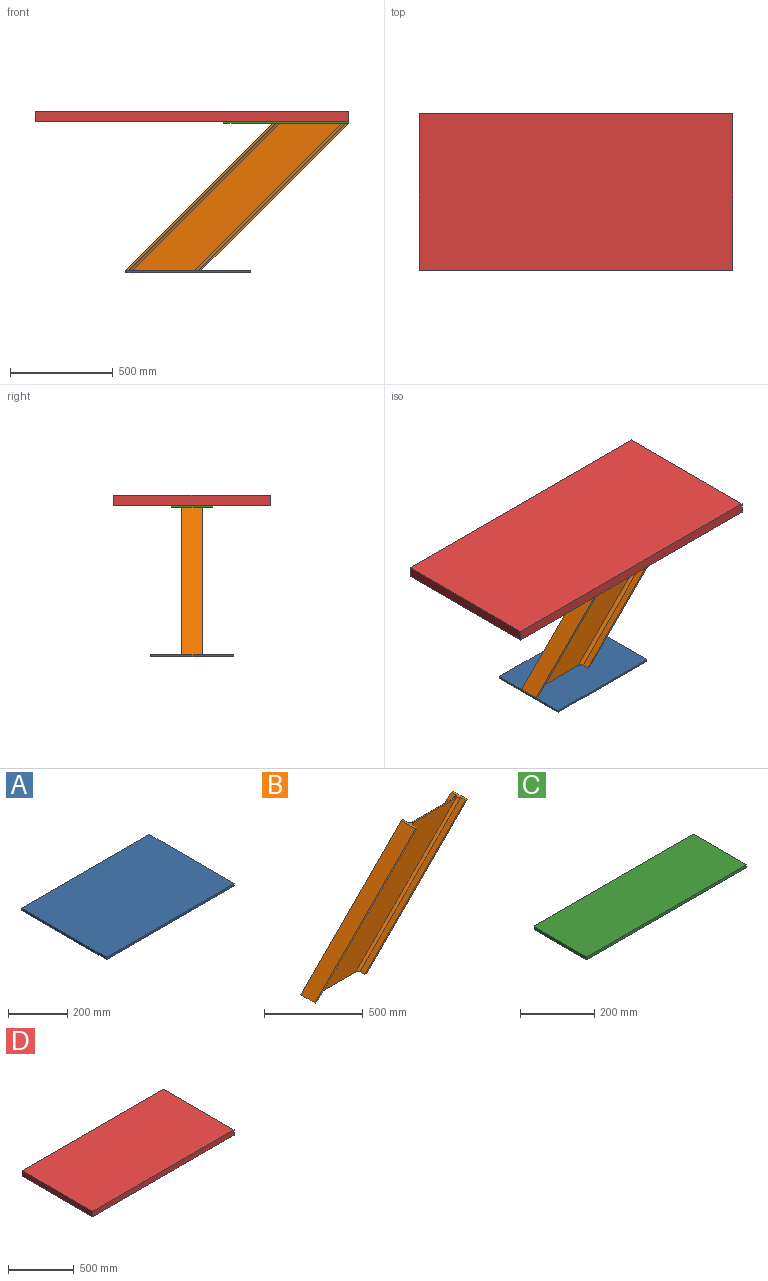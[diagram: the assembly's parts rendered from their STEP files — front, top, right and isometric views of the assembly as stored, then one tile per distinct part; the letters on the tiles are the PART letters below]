
ASSEMBLY  parts=4 mates=3
PART A: 10 faces, bbox 609.6x406.4x9.5 mm
  f0: plane 400.05x9.53mm, normal (1,0,0), area 3810.5mm2, adj f1,f7,f8,f9
  f1: cylinder r=3.17mm len=9.53mm, axis (0,0,-1), area 47.5mm2, adj f0,f2,f8,f9
  f2: plane 603.25x9.53mm, normal (0,1,0), area 5746mm2, adj f1,f3,f8,f9
  f3: cylinder r=3.17mm len=9.53mm, axis (0,0,-1), area 47.5mm2, adj f2,f4,f8,f9
  f4: plane 400.05x9.53mm, normal (-1,0,0), area 3810.5mm2, adj f3,f5,f8,f9
  f5: cylinder r=3.17mm len=9.53mm, axis (0,0,-1), area 47.5mm2, adj f4,f6,f8,f9
  f6: plane 603.25x9.53mm, normal (0,-1,0), area 5746mm2, adj f5,f7,f8,f9
  f7: cylinder r=3.17mm len=9.53mm, axis (0,0,-1), area 47.5mm2, adj f0,f6,f8,f9
  f8: plane 609.6x406.4mm, normal (0,0,1), area 247732.8mm2, adj f0,f1,f2,f3,f4,f5,f6,f7
  f9: plane 609.6x406.4mm, normal (0,0,-1), area 247732.8mm2, adj f0,f1,f2,f3,f4,f5,f6,f7
PART B: 19 faces, bbox 1086.6x101.6x738.6 mm
  f0: cylinder r=14.29mm len=738.63mm, axis (0.71,0,0.71), area 22801.8mm2, adj f1,f16,f17,f18
  f1: plane 1019.26x718.42mm, normal (0,1,0), area 216128.6mm2, adj f0,f2,f17,f18
  f2: cylinder r=14.29mm len=738.63mm, axis (0.71,0,0.71), area 22801.8mm2, adj f1,f3,f17,f18
  f3: plane 718.42x718.42mm, normal (0.71,0,-0.71), area 32245.1mm2, adj f2,f4,f17,f18
  f4: cylinder r=1.6mm len=720.68mm, axis (0.71,0,0.71), area 2553.8mm2, adj f3,f5,f17,f18
  f5: plane 729.63x718.42mm, normal (0,1,0), area 8051.6mm2, adj f4,f6,f17,f18
  f6: plane 718.42x718.42mm, normal (-0.71,0,0.71), area 103225.6mm2, adj f5,f7,f17,f18
  f7: plane 731.89x718.42mm, normal (0,-1,0), area 9677.4mm2, adj f6,f8,f17,f18
  f8: plane 718.42x718.42mm, normal (0.71,0,-0.71), area 33870.9mm2, adj f7,f9,f17,f18
  f9: cylinder r=14.29mm len=738.63mm, axis (0.71,0,0.71), area 22801.8mm2, adj f8,f10,f17,f18
  f10: plane 1019.24x718.42mm, normal (0,-1,0), area 216115.7mm2, adj f9,f11,f17,f18
  f11: cylinder r=14.3mm len=738.64mm, axis (0.71,0,0.71), area 22822.1mm2, adj f10,f12,f17,f18
  f12: plane 718.42x718.42mm, normal (-0.71,0,0.71), area 33858mm2, adj f11,f13,f17,f18
  f13: plane 731.89x718.42mm, normal (0,-1,0), area 9677.4mm2, adj f12,f14,f17,f18
  f14: plane 718.42x718.42mm, normal (0.71,0,-0.71), area 103225.6mm2, adj f13,f15,f17,f18
  f15: plane 731.89x718.42mm, normal (0,1,0), area 9677.4mm2, adj f14,f16,f17,f18
  f16: plane 718.42x718.42mm, normal (-0.71,0,0.71), area 33870.9mm2, adj f0,f15,f17,f18
  f17: plane 368.19x101.6mm, normal (0,0,-1), area 5151.3mm2, adj f0,f1,f2,f3,f4,f5,f6,f7
  f18: plane 368.19x101.6mm, normal (0,0,1), area 5151.3mm2, adj f0,f1,f2,f3,f4,f5,f6,f7
PART C: 10 faces, bbox 609.6x203.2x9.5 mm
  f0: plane 196.85x9.53mm, normal (-1,0,0), area 1875mm2, adj f1,f7,f8,f9
  f1: cylinder r=3.17mm len=9.53mm, axis (0,0,-1), area 47.5mm2, adj f0,f2,f8,f9
  f2: plane 603.25x9.53mm, normal (0,-1,0), area 5746mm2, adj f1,f3,f8,f9
  f3: cylinder r=3.17mm len=9.53mm, axis (0,0,-1), area 47.5mm2, adj f2,f4,f8,f9
  f4: plane 196.85x9.53mm, normal (1,0,0), area 1875mm2, adj f3,f5,f8,f9
  f5: cylinder r=3.17mm len=9.53mm, axis (0,0,-1), area 47.5mm2, adj f4,f6,f8,f9
  f6: plane 603.25x9.53mm, normal (0,1,0), area 5746mm2, adj f5,f7,f8,f9
  f7: cylinder r=3.17mm len=9.53mm, axis (0,0,-1), area 47.5mm2, adj f0,f6,f8,f9
  f8: plane 609.6x203.2mm, normal (0,0,1), area 123862.1mm2, adj f0,f1,f2,f3,f4,f5,f6,f7
  f9: plane 609.6x203.2mm, normal (0,0,-1), area 123862.1mm2, adj f0,f1,f2,f3,f4,f5,f6,f7
PART D: 6 faces, bbox 1524x762x50.8 mm
  f0: plane 1524x50.8mm, normal (0,1,0), area 77419.2mm2, adj f1,f3,f4,f5
  f1: plane 762x50.8mm, normal (-1,0,0), area 38709.6mm2, adj f0,f2,f4,f5
  f2: plane 1524x50.8mm, normal (0,-1,0), area 77419.2mm2, adj f1,f3,f4,f5
  f3: plane 762x50.8mm, normal (1,0,0), area 38709.6mm2, adj f0,f2,f4,f5
  f4: plane 1524x762mm, normal (0,0,1), area 1161288mm2, adj f0,f1,f2,f3
  f5: plane 1524x762mm, normal (0,0,-1), area 1161288mm2, adj f0,f1,f2,f3
PLACE A t=(-804.35,-33.3,-737.47)mm
PLACE B t=(-285.85,3.17,-9.52)mm
PLACE C t=(-609.6,-101.6,-9.52)mm
PLACE D t=(-774.03,-97.75,0)mm
MATE fastened B.f18 <-> C.f9  axis (0,0,1) through (0,0,-9.52)mm
MATE fastened D.f5 <-> C.f8  axis (0,0,-1) through (0,0,0)mm
MATE fastened B.f17 <-> A.f8  axis (0,0,-1) through (-1086.61,0,-727.95)mm
